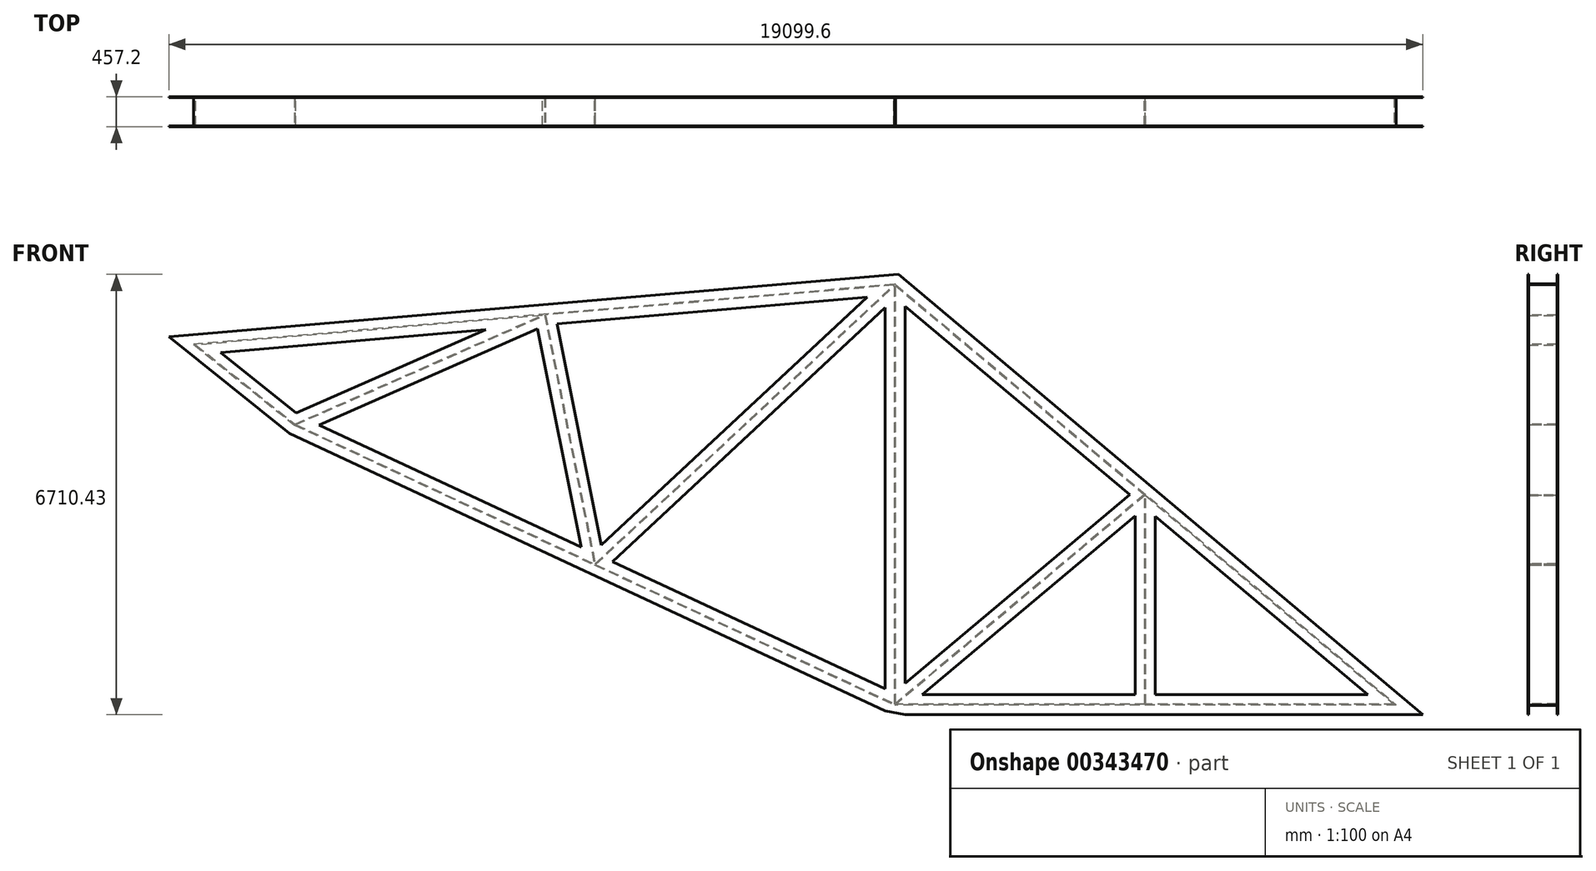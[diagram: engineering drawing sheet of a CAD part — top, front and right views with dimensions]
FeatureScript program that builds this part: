
annotation { "Feature Type Name" : "Feature", "Feature Type Description" : "" }
export const myFeature = defineFeature(function(context is Context, id is Id, definition is map)
    precondition{}
    {
        {
            var Q0;
            Q0=qCreatedBy(makeId("Front.planeOp"),FACE);
            var sketch = newSketch(context, id + "F0", { "sketchPlane" : qUnion([Q0])});
            skLineSegment(sketch, "E0", {"start": v(0, 0) * mm, "end": v(3810, 0) * mm});
            skLineSegment(sketch, "E1", {"start": v(3810, 0) * mm, "end": v(7620, 0) * mm});
            skLineSegment(sketch, "E2", {"start": v(7620, 0) * mm, "end": v(0, 6400.8) * mm});
            skLineSegment(sketch, "E3", {"start": v(0, 6400.8) * mm, "end": v(0, 0) * mm});
            skLineSegment(sketch, "E4", {"start": v(3810, 0) * mm, "end": v(3810, 3200.4) * mm});
            skLineSegment(sketch, "E5", {"start": v(3810, 3200.4) * mm, "end": v(0, 0) * mm});
            skLineSegment(sketch, "E6", {"start": v(0, 0) * mm, "end": v(-4571.76, 2133.8) * mm});
            skLineSegment(sketch, "E7", {"start": v(-4571.76, 2133.8) * mm, "end": v(0, 6400.8) * mm});
            skLineSegment(sketch, "E8", {"start": v(0, 6400.8) * mm, "end": v(-5334, 5943.52) * mm});
            skLineSegment(sketch, "E9", {"start": v(0, 6400.8) * mm, "end": v(-16005.4, 6400.8) * mm, "construction": true});
            skLineSegment(sketch, "E10", {"start": v(-5334, 5943.52) * mm, "end": v(-4571.76, 2133.8) * mm});
            skLineSegment(sketch, "E11", {"start": v(-5334, 5943.52) * mm, "end": v(-10667.98, 5486.23) * mm});
            skLineSegment(sketch, "E12", {"start": v(-4571.76, 2133.8) * mm, "end": v(-9143.52, 4267.58) * mm});
            skLineSegment(sketch, "E13", {"start": v(-9143.52, 4267.58) * mm, "end": v(-5334, 5943.52) * mm});
            skLineSegment(sketch, "E14", {"start": v(-9143.52, 4267.58) * mm, "end": v(-10667.98, 5486.23) * mm});
            skSolve(sketch);
        }
        {
            var Q0;
            Q0=qCreatedBy(makeId("Top.planeOp"),FACE);
            var sketch = newSketch(context, id + "F1", { "sketchPlane" : qUnion([Q0])});
            skLineSegment(sketch, "E15.bottom", {"start": v(6.35, -228.6) * mm, "end": v(-6.35, -228.6) * mm});
            skLineSegment(sketch, "E15.top", {"start": v(6.35, 228.6) * mm, "end": v(-6.35, 228.6) * mm});
            skLineSegment(sketch, "E15.left", {"start": v(6.35, -215.9) * mm, "end": v(6.35, 215.9) * mm});
            skLineSegment(sketch, "E15.right", {"start": v(-6.35, -215.9) * mm, "end": v(-6.35, 215.9) * mm});
            skPoint(sketch, "E15.middle", {"position": v(0, 0) * mm});
            skLineSegment(sketch, "E16.bottom", {"start": v(152.4, -228.6) * mm, "end": v(6.35, -228.6) * mm});
            skLineSegment(sketch, "E16.top", {"start": v(152.4, -215.9) * mm, "end": v(6.35, -215.9) * mm});
            skLineSegment(sketch, "E16.left", {"start": v(152.4, -228.6) * mm, "end": v(152.4, -215.9) * mm});
            skLineSegment(sketch, "E16.right", {"start": v(-152.4, -228.6) * mm, "end": v(-152.4, -215.9) * mm});
            skLineSegment(sketch, "E17.trimOffspring", {"start": v(-6.35, -228.6) * mm, "end": v(-152.4, -228.6) * mm});
            skLineSegment(sketch, "E18.trimOffspring", {"start": v(-6.35, -215.9) * mm, "end": v(-152.4, -215.9) * mm});
            skLineSegment(sketch, "E19.MirrorCS", {"start": v(-152.4, 228.6) * mm, "end": v(-152.4, 215.9) * mm});
            skLineSegment(sketch, "E20.MirrorCS", {"start": v(-6.35, 228.6) * mm, "end": v(-152.4, 228.6) * mm});
            skLineSegment(sketch, "E21.MirrorCS", {"start": v(-6.35, 215.9) * mm, "end": v(-152.4, 215.9) * mm});
            skLineSegment(sketch, "E22.MirrorCS", {"start": v(152.4, 228.6) * mm, "end": v(152.4, 215.9) * mm});
            skLineSegment(sketch, "E23.MirrorCS", {"start": v(152.4, 228.6) * mm, "end": v(6.35, 228.6) * mm});
            skLineSegment(sketch, "E24.MirrorCS", {"start": v(152.4, 215.9) * mm, "end": v(6.35, 215.9) * mm});
            skSolve(sketch);
        }
        {
            var Q0;
            Q0 = qSketchRegion(id + "F1", true);
            var Q1;
            Q1=sQuery(id+"F0.wireOp",EDGE,"E3");
            var Q2;
            Q2=sQuery(id+"F0.wireOp",EDGE,"E8");
            var Q3;
            Q3=sQuery(id+"F0.wireOp",EDGE,"E11");
            var Q4;
            Q4=sQuery(id+"F0.wireOp",EDGE,"E14");
            var Q5;
            Q5=sQuery(id+"F0.wireOp",EDGE,"E12");
            var Q6;
            Q6=sQuery(id+"F0.wireOp",EDGE,"E6");
            sweep(context, id + "F2", {"profiles" : qUnion([Q0]), "path" : qUnion([Q1, Q2, Q3, Q4, Q5, Q6])});
        }
        {
            var Q0;
            Q0 = qSketchRegion(id + "F1", true);
            var Q1;
            Q1=sQuery(id+"F0.wireOp",EDGE,"E3");
            var Q2;
            Q2=sQuery(id+"F0.wireOp",EDGE,"E2");
            var Q3;
            Q3=sQuery(id+"F0.wireOp",EDGE,"E1");
            var Q4;
            Q4=sQuery(id+"F0.wireOp",EDGE,"E0");
            sweep(context, id + "F3", {"operationType" : NewBodyOperationType.ADD, "profiles" : qUnion([Q0]), "path" : qUnion([Q1, Q2, Q3, Q4])});
        }
        {
            var Q0;
            {var subQ0=sQuery(id+"F0.wireOp",EDGE,"E3");var subQ1=sQuery(id+"F1.wireOp",EDGE,"E15.right");Q0=makeQuery(id+"F3.boolean.opBoolean","SPLIT",FACE,{"disambiguationData":[TD([makeQuery(id+"F2.opSweep","SWEPT_FACE",FACE,{"disambiguationData":[OSD([subQ0,sQuery(id+"F1.wireOp",EDGE,"E15.left")])]})])],"derivedFrom":makeQuery(id+"F3.opSweep","SWEPT_FACE",FACE,{"disambiguationData":[OSD([sQuery(id+"F0.wireOp",EDGE,"E2"),subQ1])]})});}
            var sketch = newSketch(context, id + "F4", { "sketchPlane" : qUnion([Q0])});
            skLineSegment(sketch, "E25.bottom", {"start": v(865.21, -228.6) * mm, "end": v(852.51, -228.6) * mm});
            skLineSegment(sketch, "E25.top", {"start": v(865.21, 228.6) * mm, "end": v(852.51, 228.6) * mm});
            skLineSegment(sketch, "E25.left", {"start": v(865.21, -215.9) * mm, "end": v(865.21, 215.9) * mm});
            skLineSegment(sketch, "E25.right", {"start": v(852.51, -215.9) * mm, "end": v(852.51, 215.9) * mm});
            skPoint(sketch, "E25.middle", {"position": v(858.86, 0) * mm});
            skLineSegment(sketch, "E26.bottom", {"start": v(1011.26, -228.6) * mm, "end": v(865.21, -228.6) * mm});
            skLineSegment(sketch, "E26.top", {"start": v(1011.26, -215.9) * mm, "end": v(865.21, -215.9) * mm});
            skLineSegment(sketch, "E26.left", {"start": v(1011.26, -228.6) * mm, "end": v(1011.26, -215.9) * mm});
            skLineSegment(sketch, "E26.right", {"start": v(706.46, -228.6) * mm, "end": v(706.46, -215.9) * mm});
            skLineSegment(sketch, "E27.trimOffspring", {"start": v(852.51, -228.6) * mm, "end": v(706.46, -228.6) * mm});
            skLineSegment(sketch, "E28.trimOffspring", {"start": v(852.51, -215.9) * mm, "end": v(706.46, -215.9) * mm});
            skLineSegment(sketch, "E29.MirrorCS", {"start": v(706.46, 228.6) * mm, "end": v(706.46, 215.9) * mm});
            skLineSegment(sketch, "E30.MirrorCS", {"start": v(852.51, 228.6) * mm, "end": v(706.46, 228.6) * mm});
            skLineSegment(sketch, "E31.MirrorCS", {"start": v(852.51, 215.9) * mm, "end": v(706.46, 215.9) * mm});
            skLineSegment(sketch, "E32.MirrorCS", {"start": v(1011.26, 228.6) * mm, "end": v(1011.26, 215.9) * mm});
            skLineSegment(sketch, "E33.MirrorCS", {"start": v(1011.26, 228.6) * mm, "end": v(865.21, 228.6) * mm});
            skLineSegment(sketch, "E34.MirrorCS", {"start": v(1011.26, 215.9) * mm, "end": v(865.21, 215.9) * mm});
            skSolve(sketch);
        }
        {
            var Q0;
            Q0 = qSketchRegion(id + "F4", true);
            var Q1;
            Q1=sQuery(id+"F0.wireOp",EDGE,"E5");
            sweep(context, id + "F5", {"operationType" : NewBodyOperationType.ADD, "profiles" : qUnion([Q0]), "path" : qUnion([Q1])});
        }
        {
            var Q0;
            {var subQ0=sQuery(id+"F1.wireOp",EDGE,"E15.right");var subQ1=sQuery(id+"F0.wireOp",EDGE,"E3");Q0=makeQuery(id+"F3.boolean.opBoolean","SPLIT",FACE,{"disambiguationData":[TD([makeQuery(id+"F2.opSweep","SWEPT_FACE",FACE,{"disambiguationData":[OSD([subQ1,sQuery(id+"F1.wireOp",EDGE,"E15.left")])]})])],"derivedFrom":makeQuery(id+"F3.opSweep","SWEPT_FACE",FACE,{"disambiguationData":[OSD([sQuery(id+"F0.wireOp",EDGE,"E0"),subQ0])]})});}
            var sketch = newSketch(context, id + "F6", { "sketchPlane" : qUnion([Q0])});
            skLineSegment(sketch, "E35.bottom", {"start": v(3816.35, -228.6) * mm, "end": v(3803.65, -228.6) * mm});
            skLineSegment(sketch, "E35.top", {"start": v(3816.35, 228.6) * mm, "end": v(3803.65, 228.6) * mm});
            skLineSegment(sketch, "E35.left", {"start": v(3816.35, -215.9) * mm, "end": v(3816.35, 215.9) * mm});
            skLineSegment(sketch, "E35.right", {"start": v(3803.65, -215.9) * mm, "end": v(3803.65, 215.9) * mm});
            skPoint(sketch, "E35.middle", {"position": v(3810, 0) * mm});
            skLineSegment(sketch, "E36.bottom", {"start": v(3962.4, -228.6) * mm, "end": v(3816.35, -228.6) * mm});
            skLineSegment(sketch, "E36.top", {"start": v(3962.4, -215.9) * mm, "end": v(3816.35, -215.9) * mm});
            skLineSegment(sketch, "E36.left", {"start": v(3962.4, -228.6) * mm, "end": v(3962.4, -215.9) * mm});
            skLineSegment(sketch, "E36.right", {"start": v(3657.6, -228.6) * mm, "end": v(3657.6, -215.9) * mm});
            skLineSegment(sketch, "E37.trimOffspring", {"start": v(3803.65, -228.6) * mm, "end": v(3657.6, -228.6) * mm});
            skLineSegment(sketch, "E38.trimOffspring", {"start": v(3803.65, -215.9) * mm, "end": v(3657.6, -215.9) * mm});
            skLineSegment(sketch, "E39.MirrorCS", {"start": v(3657.6, 228.6) * mm, "end": v(3657.6, 215.9) * mm});
            skLineSegment(sketch, "E40.MirrorCS", {"start": v(3803.65, 228.6) * mm, "end": v(3657.6, 228.6) * mm});
            skLineSegment(sketch, "E41.MirrorCS", {"start": v(3803.65, 215.9) * mm, "end": v(3657.6, 215.9) * mm});
            skLineSegment(sketch, "E42.MirrorCS", {"start": v(3962.4, 228.6) * mm, "end": v(3962.4, 215.9) * mm});
            skLineSegment(sketch, "E43.MirrorCS", {"start": v(3962.4, 228.6) * mm, "end": v(3816.35, 228.6) * mm});
            skLineSegment(sketch, "E44.MirrorCS", {"start": v(3962.4, 215.9) * mm, "end": v(3816.35, 215.9) * mm});
            skSolve(sketch);
        }
        {
            var Q0;
            Q0 = qSketchRegion(id + "F6", true);
            var Q1;
            Q1=sQuery(id+"F0.wireOp",EDGE,"E4");
            sweep(context, id + "F7", {"operationType" : NewBodyOperationType.ADD, "profiles" : qUnion([Q0]), "path" : qUnion([Q1])});
        }
        {
            var Q0;
            {var subQ1=sQuery(id+"F1.wireOp",EDGE,"E15.left");Q0=makeQuery(id+"F3.boolean.opBoolean","SPLIT",FACE,{"disambiguationData":[TD([makeQuery(id+"F2.opSweep","SWEPT_FACE",FACE,{"disambiguationData":[OSD([sQuery(id+"F0.wireOp",EDGE,"E14"),subQ1])]})])],"derivedFrom":makeQuery(id+"F2.opSweep","SWEPT_FACE",FACE,{"disambiguationData":[OSD([sQuery(id+"F0.wireOp",EDGE,"E11"),subQ1])]})});}
            var sketch = newSketch(context, id + "F8", { "sketchPlane" : qUnion([Q0])});
            skLineSegment(sketch, "E45.bottom", {"start": v(-4800.47, -228.6) * mm, "end": v(-4813.17, -228.6) * mm});
            skLineSegment(sketch, "E45.left", {"start": v(-4800.47, -215.9) * mm, "end": v(-4800.47, 215.9) * mm});
            skLineSegment(sketch, "E45.right", {"start": v(-4813.17, -215.9) * mm, "end": v(-4813.17, 215.9) * mm});
            skPoint(sketch, "E45.middle", {"position": v(-4806.82, 0) * mm});
            skLineSegment(sketch, "E46.bottom", {"start": v(-4654.42, -228.6) * mm, "end": v(-4800.47, -228.6) * mm});
            skLineSegment(sketch, "E46.top", {"start": v(-4654.42, -215.9) * mm, "end": v(-4800.47, -215.9) * mm});
            skLineSegment(sketch, "E46.left", {"start": v(-4654.42, -228.6) * mm, "end": v(-4654.42, -215.9) * mm});
            skLineSegment(sketch, "E46.right", {"start": v(-4959.22, -228.6) * mm, "end": v(-4959.22, -215.9) * mm});
            skLineSegment(sketch, "E47.trimOffspring", {"start": v(-4813.17, -228.6) * mm, "end": v(-4959.22, -228.6) * mm});
            skLineSegment(sketch, "E48.trimOffspring", {"start": v(-4813.17, -215.9) * mm, "end": v(-4959.22, -215.9) * mm});
            skLineSegment(sketch, "E49.MirrorCS", {"start": v(-4959.22, 228.6) * mm, "end": v(-4959.22, 215.9) * mm});
            skLineSegment(sketch, "E50.MirrorCS", {"start": v(-4806.82, 228.6) * mm, "end": v(-4959.22, 228.6) * mm});
            skLineSegment(sketch, "E51.MirrorCS", {"start": v(-4813.17, 215.9) * mm, "end": v(-4959.22, 215.9) * mm});
            skLineSegment(sketch, "E52.MirrorCS", {"start": v(-4654.42, 228.6) * mm, "end": v(-4654.42, 215.9) * mm});
            skLineSegment(sketch, "E53.MirrorCS", {"start": v(-4654.42, 228.6) * mm, "end": v(-4806.82, 228.6) * mm});
            skLineSegment(sketch, "E54.MirrorCS", {"start": v(-4654.42, 215.9) * mm, "end": v(-4800.47, 215.9) * mm});
            skSolve(sketch);
        }
        {
            var Q0;
            Q0 = qSketchRegion(id + "F8", true);
            var Q1;
            Q1=sQuery(id+"F0.wireOp",EDGE,"E10");
            var Q2;
            Q2=sQuery(id+"F0.wireOp",EDGE,"E7");
            sweep(context, id + "F9", {"operationType" : NewBodyOperationType.ADD, "profiles" : qUnion([Q0]), "path" : qUnion([Q1, Q2])});
        }
        {
            var Q0;
            Q0=sQuery(id+"F0.wireOp",EDGE,"E13");
            var Q1;
            Q1=sQuery(id+"F0.wireOp",VERTEX,"E12.end");
            cPlane(context, id + "F10", {"entities" : qUnion([Q0, Q1]), "cplaneType" : CPlaneType.LINE_POINT, "offset" : 25.4 * mm, "width" : 152.4 * mm, "height" : 152.4 * mm});
        }
        {
            var Q0;
            Q0=qCreatedBy(id+"F10.planeOp",FACE);
            var sketch = newSketch(context, id + "F11", { "sketchPlane" : qUnion([Q0])});
            skLineSegment(sketch, "E55.bottom", {"start": v(228.6, 7594.6) * mm, "end": v(228.6, 7581.9) * mm});
            skLineSegment(sketch, "E55.top", {"start": v(-228.6, 7594.6) * mm, "end": v(-228.6, 7581.9) * mm});
            skLineSegment(sketch, "E55.left", {"start": v(215.9, 7594.6) * mm, "end": v(-215.9, 7594.6) * mm});
            skLineSegment(sketch, "E55.right", {"start": v(215.9, 7581.9) * mm, "end": v(-215.9, 7581.9) * mm});
            skPoint(sketch, "E55.middle", {"position": v(0, 7588.25) * mm});
            skLineSegment(sketch, "E56.bottom", {"start": v(228.6, 7740.65) * mm, "end": v(228.6, 7594.6) * mm});
            skLineSegment(sketch, "E56.top", {"start": v(215.9, 7740.65) * mm, "end": v(215.9, 7594.6) * mm});
            skLineSegment(sketch, "E56.left", {"start": v(228.6, 7740.65) * mm, "end": v(215.9, 7740.65) * mm});
            skLineSegment(sketch, "E56.right", {"start": v(228.6, 7435.85) * mm, "end": v(215.9, 7435.85) * mm});
            skLineSegment(sketch, "E57.trimOffspring", {"start": v(228.6, 7581.9) * mm, "end": v(228.6, 7435.85) * mm});
            skLineSegment(sketch, "E58.trimOffspring", {"start": v(215.9, 7581.9) * mm, "end": v(215.9, 7435.85) * mm});
            skLineSegment(sketch, "E59.MirrorCS", {"start": v(-228.6, 7435.85) * mm, "end": v(-215.9, 7435.85) * mm});
            skLineSegment(sketch, "E60.MirrorCS", {"start": v(-228.6, 7581.9) * mm, "end": v(-228.6, 7435.85) * mm});
            skLineSegment(sketch, "E61.MirrorCS", {"start": v(-215.9, 7581.9) * mm, "end": v(-215.9, 7435.85) * mm});
            skLineSegment(sketch, "E62.MirrorCS", {"start": v(-228.6, 7740.65) * mm, "end": v(-215.9, 7740.65) * mm});
            skLineSegment(sketch, "E63.MirrorCS", {"start": v(-228.6, 7740.65) * mm, "end": v(-228.6, 7594.6) * mm});
            skLineSegment(sketch, "E64.MirrorCS", {"start": v(-215.9, 7740.65) * mm, "end": v(-215.9, 7594.6) * mm});
            skSolve(sketch);
        }
        {
            var Q0;
            {var subQ0=sQuery(id+"F1.wireOp",EDGE,"E23.MirrorCS");var subQ1=sQuery(id+"F1.wireOp",EDGE,"E20.MirrorCS");var subQ2=sQuery(id+"F1.wireOp",EDGE,"E15.top");Q0=makeQuery(id+"FeVoyphotTu8DCG_1.boolean.opBoolean","MERGE",FACE,{"derivedFrom":[makeQuery(id+"Fxf88pbwrwBp0e5_1.boolean.opBoolean","MERGE",FACE,{"derivedFrom":[makeQuery(id+"F2.opSweep","SWEPT_FACE",FACE,{"disambiguationData":[OSD([sQuery(id+"F0.wireOp",EDGE,"E12"),subQ2,subQ1,subQ0])]}),makeQuery(id+"Fxf88pbwrwBp0e5_1.opSweep","SWEPT_FACE",FACE,{"disambiguationData":[OSD([sQuery(id+"F0.wireOp",EDGE,"E5"),subQ2,subQ1,subQ0])]})]}),makeQuery(id+"FeVoyphotTu8DCG_1.opSweep","SWEPT_FACE",FACE,{"disambiguationData":[OSD([sQuery(id+"F0.wireOp",EDGE,"E3"),subQ2,subQ1,subQ0])]})]});}
            var sketch = newSketch(context, id + "F12", { "sketchPlane" : qUnion([Q0])});
            skLineSegment(sketch, "E65.0", {"start": v(-152.4, 6471.82) * mm, "end": v(-8038.37, -152.4) * mm});
            skLineSegment(sketch, "E66.0", {"start": v(-8038.37, -152.4) * mm, "end": v(-152.4, -152.4) * mm});
            skLineSegment(sketch, "E67.0", {"start": v(4544.61, 1952.94) * mm, "end": v(152.4, -97.05) * mm});
            skLineSegment(sketch, "E68.0", {"start": v(9224.47, 4137.18) * mm, "end": v(4704.2, 2027.42) * mm});
            skLineSegment(sketch, "E69.0", {"start": v(11061.23, 5605.48) * mm, "end": v(9224.47, 4137.18) * mm});
            skLineSegment(sketch, "E70.0", {"start": v(152.4, 6540.7) * mm, "end": v(11061.23, 5605.48) * mm});
            skLineSegment(sketch, "E71", {"start": v(4704.2, 2027.42) * mm, "end": v(4544.61, 1952.94) * mm});
            skLineSegment(sketch, "E72", {"start": v(152.4, -97.05) * mm, "end": v(-152.4, -152.4) * mm});
            skLineSegment(sketch, "E73", {"start": v(-152.4, 6471.82) * mm, "end": v(-49.77, 6558.03) * mm});
            skLineSegment(sketch, "E74", {"start": v(152.4, 6540.7) * mm, "end": v(-49.77, 6558.03) * mm});
            skPoint(sketch, "E75.orphan", {"position": v(-2030.66, 6727.85) * mm});
            skLineSegment(sketch, "E76.bottom", {"start": v(14540.58, 9424.63) * mm, "end": v(-18668.37, 9424.63) * mm});
            skLineSegment(sketch, "E76.top", {"start": v(14540.58, -7009.48) * mm, "end": v(-18668.37, -7009.48) * mm});
            skLineSegment(sketch, "E76.left", {"start": v(14540.58, 9424.63) * mm, "end": v(14540.58, -7009.48) * mm});
            skLineSegment(sketch, "E76.right", {"start": v(-18668.37, 9424.63) * mm, "end": v(-18668.37, -7009.48) * mm});
            skSolve(sketch);
        }
        {
            var Q0;
            Q0 = qSketchRegion(id + "F11", true);
            var Q1;
            Q1=sQuery(id+"F0.wireOp",EDGE,"E13");
            sweep(context, id + "F13", {"operationType" : NewBodyOperationType.ADD, "profiles" : qUnion([Q0]), "path" : qUnion([Q1])});
        }
        {
            var Q0;
            Q0 = qSketchRegion(id + "F12", true);
            extrude(context, id + "F14", {"entities" : qUnion([Q0]), "operationType" : NewBodyOperationType.REMOVE, "endBound" : BoundingType.SYMMETRIC, "oppositeDirection" : true, "depth" : 1270 * mm});
        }
    });
